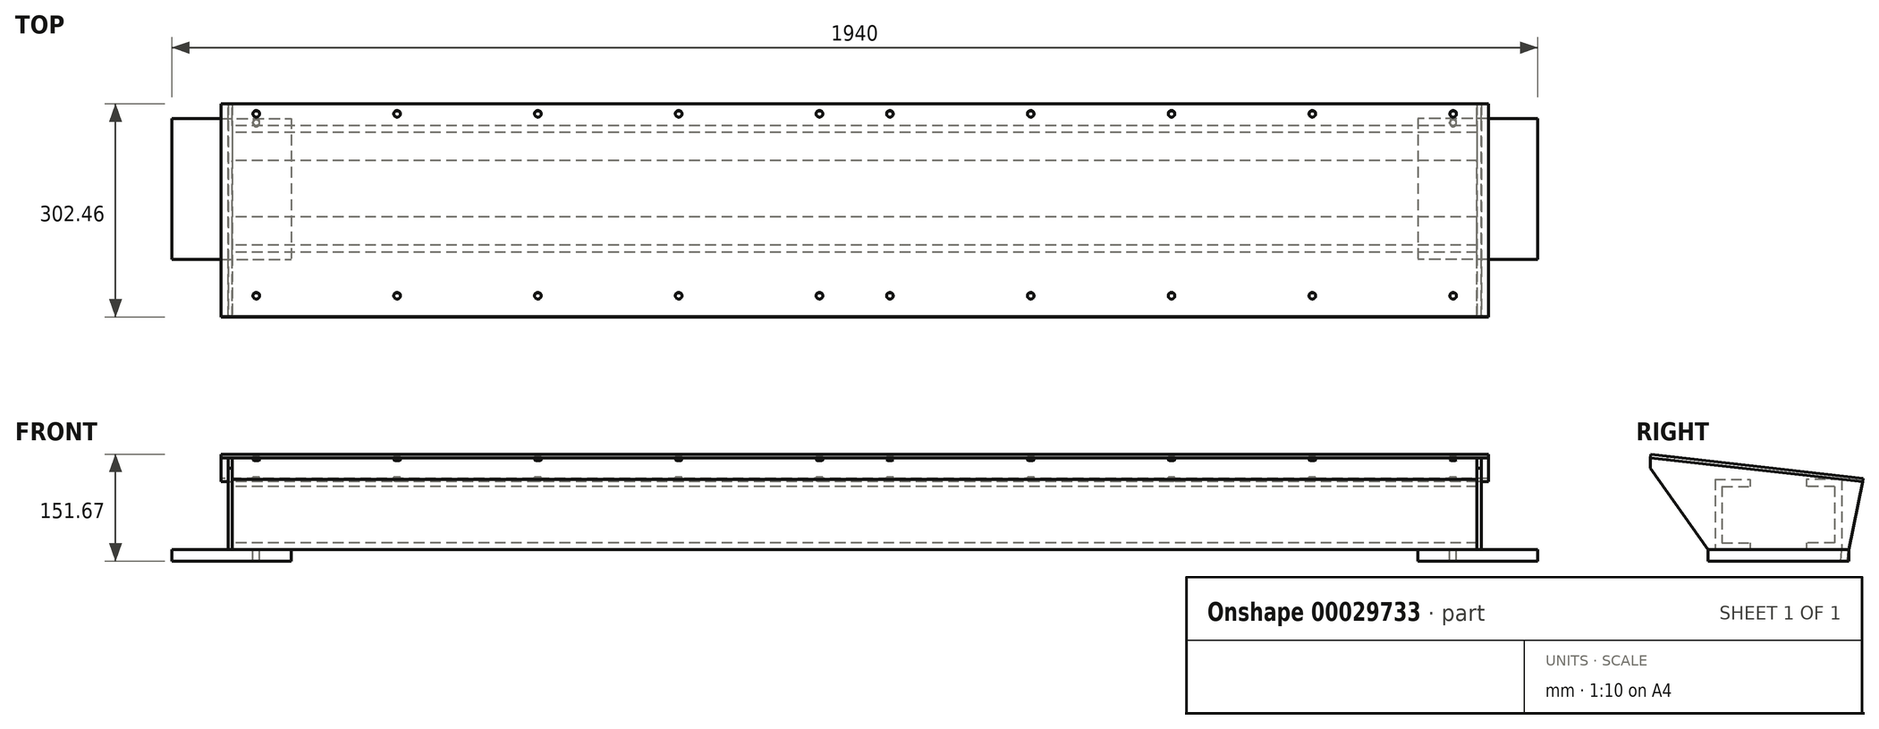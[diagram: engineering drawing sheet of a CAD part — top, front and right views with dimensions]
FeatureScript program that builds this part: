
annotation { "Feature Type Name" : "Feature", "Feature Type Description" : "" }
export const myFeature = defineFeature(function(context is Context, id is Id, definition is map)
    precondition{}
    {
        {
            var Q0;
            Q0=qCreatedBy(makeId("Top.planeOp"),FACE);
            var sketch = newSketch(context, id + "F0", { "sketchPlane" : qUnion([Q0])});
            skLineSegment(sketch, "E0", {"start": v(0, 85.67) * mm, "end": v(0, -88.89) * mm, "construction": true});
            skLineSegment(sketch, "E1.0", {"start": v(-800, 85.67) * mm, "end": v(-800, -88.89) * mm, "construction": true});
            skLineSegment(sketch, "E2.0", {"start": v(-970, 85.67) * mm, "end": v(-970, -88.89) * mm, "construction": true});
            skLineSegment(sketch, "E3", {"start": v(0, 0) * mm, "end": v(-970, 0) * mm, "construction": true});
            skLineSegment(sketch, "E4.0", {"start": v(0, 100) * mm, "end": v(-970, 100) * mm, "construction": true});
            skLineSegment(sketch, "E5.bottom", {"start": v(-970, 100) * mm, "end": v(-800, 100) * mm});
            skLineSegment(sketch, "E5.top", {"start": v(-970, -100) * mm, "end": v(-800, -100) * mm});
            skLineSegment(sketch, "E5.left", {"start": v(-970, 100) * mm, "end": v(-970, -100) * mm});
            skLineSegment(sketch, "E5.right", {"start": v(-800, 100) * mm, "end": v(-800, -100) * mm});
            skLineSegment(sketch, "E6.0", {"start": v(-950, 85.67) * mm, "end": v(-950, -88.89) * mm, "construction": true});
            skLineSegment(sketch, "E7.0", {"start": v(-959.5, 85.67) * mm, "end": v(-959.5, -88.89) * mm, "construction": true});
            skLineSegment(sketch, "E8.0", {"start": v(0, 65) * mm, "end": v(-970, 65) * mm, "construction": true});
            skLineSegment(sketch, "E9.0", {"start": v(0, 85) * mm, "end": v(-970, 85) * mm, "construction": true});
            skLineSegment(sketch, "E10.MirrorCS", {"start": v(800, 85.67) * mm, "end": v(800, -88.89) * mm});
            skLineSegment(sketch, "E11.MirrorCS", {"start": v(970, 85.67) * mm, "end": v(970, -88.89) * mm});
            skLineSegment(sketch, "E12.MirrorCS", {"start": v(970, 100) * mm, "end": v(800, 100) * mm});
            skLineSegment(sketch, "E13.MirrorCS", {"start": v(970, -100) * mm, "end": v(800, -100) * mm});
            skLineSegment(sketch, "E14.MirrorCS", {"start": v(970, 100) * mm, "end": v(970, -100) * mm});
            skLineSegment(sketch, "E15.MirrorCS", {"start": v(959.5, 85.67) * mm, "end": v(959.5, -88.89) * mm});
            skLineSegment(sketch, "E16.MirrorCS", {"start": v(950, 85.67) * mm, "end": v(950, -88.89) * mm});
            skLineSegment(sketch, "E17.MirrorCS", {"start": v(800, 100) * mm, "end": v(800, -100) * mm});
            skSolve(sketch);
        }
        {
            var Q0;
            Q0 = qSketchRegion(id + "F0", true);
            extrude(context, id + "F1", {"entities" : qUnion([Q0]), "oppositeDirection" : true, "depth" : 16 * mm});
        }
        {
            var Q0;
            Q0=qCreatedBy(makeId("Right.planeOp"),FACE);
            var sketch = newSketch(context, id + "F2", { "sketchPlane" : qUnion([Q0])});
            skLineSegment(sketch, "E18", {"start": v(0, 75.8) * mm, "end": v(0, -76.42) * mm, "construction": true});
            skLineSegment(sketch, "E19.0", {"start": v(100, 0) * mm, "end": v(-100, 0) * mm, "construction": true});
            skLineSegment(sketch, "E20.0", {"start": v(90, 100) * mm, "end": v(90, -76.42) * mm, "construction": true});
            skLineSegment(sketch, "E21.0", {"start": v(100, 100) * mm, "end": v(-100, 100) * mm, "construction": true});
            skLineSegment(sketch, "E22.bottom", {"start": v(90, 100) * mm, "end": v(40, 100) * mm});
            skLineSegment(sketch, "E22.top", {"start": v(90, 0) * mm, "end": v(40, 0) * mm});
            skLineSegment(sketch, "E22.left", {"start": v(90, 100) * mm, "end": v(90, 0) * mm});
            skLineSegment(sketch, "E22.right", {"start": v(40, 100) * mm, "end": v(40, 90) * mm});
            skLineSegment(sketch, "E23.0", {"start": v(80, 90) * mm, "end": v(40, 90) * mm});
            skLineSegment(sketch, "E23.1", {"start": v(80, 90) * mm, "end": v(80, 10) * mm});
            skLineSegment(sketch, "E23.2", {"start": v(80, 10) * mm, "end": v(40, 10) * mm});
            skLineSegment(sketch, "E24.trimOffspring", {"start": v(40, 10) * mm, "end": v(40, 0) * mm});
            skLineSegment(sketch, "E25.MirrorCS", {"start": v(-40, 100) * mm, "end": v(-40, 90) * mm});
            skLineSegment(sketch, "E26.MirrorCS", {"start": v(-40, 10) * mm, "end": v(-40, 0) * mm});
            skLineSegment(sketch, "E27.MirrorCS", {"start": v(-90, 100) * mm, "end": v(-40, 100) * mm});
            skLineSegment(sketch, "E28.MirrorCS", {"start": v(-90, 100) * mm, "end": v(-90, 0) * mm});
            skLineSegment(sketch, "E29.MirrorCS", {"start": v(-80, 90) * mm, "end": v(-40, 90) * mm});
            skLineSegment(sketch, "E30.MirrorCS", {"start": v(-80, 90) * mm, "end": v(-80, 10) * mm});
            skLineSegment(sketch, "E31.MirrorCS", {"start": v(-80, 10) * mm, "end": v(-40, 10) * mm});
            skLineSegment(sketch, "E32.MirrorCS", {"start": v(-90, 0) * mm, "end": v(-40, 0) * mm});
            skSolve(sketch);
        }
        {
            var Q0;
            Q0 = qSketchRegion(id + "F2", true);
            extrude(context, id + "F3", {"entities" : qUnion([Q0]), "endBound" : BoundingType.SYMMETRIC, "depth" : 1768 * mm});
        }
        {
            var Q0;
            Q0=makeQuery(id+"F3.opExtrude","CAP_FACE",FACE,{"disambiguationData":[OSD([sQuery(id+"F2.wireOp",EDGE,"E22.bottom"),sQuery(id+"F2.wireOp",EDGE,"E22.top"),sQuery(id+"F2.wireOp",EDGE,"E22.left"),sQuery(id+"F2.wireOp",EDGE,"E22.right"),sQuery(id+"F2.wireOp",EDGE,"E23.0"),sQuery(id+"F2.wireOp",EDGE,"E23.1"),sQuery(id+"F2.wireOp",EDGE,"E23.2"),sQuery(id+"F2.wireOp",EDGE,"E24.trimOffspring")])],"isStart":true});
            var sketch = newSketch(context, id + "F4", { "sketchPlane" : qUnion([Q0])});
            skLineSegment(sketch, "E33.0", {"start": v(-120, 100) * mm, "end": v(-120, 0) * mm, "construction": true});
            skLineSegment(sketch, "E34.0", {"start": v(181.9, 130.7) * mm, "end": v(181.9, 0) * mm, "construction": true});
            skLineSegment(sketch, "E35.0", {"start": v(-100, 0) * mm, "end": v(100, 0) * mm, "construction": true});
            skLineSegment(sketch, "E36.0", {"start": v(-100, 130.7) * mm, "end": v(181.9, 130.7) * mm, "construction": true});
            skLineSegment(sketch, "E37.0", {"start": v(-120, 96.6) * mm, "end": v(100, 96.6) * mm, "construction": true});
            skLineSegment(sketch, "E38", {"start": v(-120, 96.6) * mm, "end": v(181.9, 130.7) * mm, "construction": true});
            skLineSegment(sketch, "E39", {"start": v(181.9, 130.7) * mm, "end": v(224.8, 130.7) * mm, "construction": true});
            skLineSegment(sketch, "E40.0", {"start": v(181.9, 115.7) * mm, "end": v(224.8, 115.7) * mm, "construction": true});
            skLineSegment(sketch, "E41", {"start": v(-100, 0) * mm, "end": v(-120, 96.6) * mm});
            skLineSegment(sketch, "E42", {"start": v(-120, 96.6) * mm, "end": v(181.9, 130.7) * mm});
            skLineSegment(sketch, "E43", {"start": v(181.9, 130.7) * mm, "end": v(181.9, 115.7) * mm});
            skLineSegment(sketch, "E44", {"start": v(181.9, 115.7) * mm, "end": v(100, 0) * mm});
            skLineSegment(sketch, "E45", {"start": v(100, 0) * mm, "end": v(-100, 0) * mm});
            skSolve(sketch);
        }
        {
            var Q0;
            Q0 = qSketchRegion(id + "F4", true);
            extrude(context, id + "F5", {"entities" : qUnion([Q0]), "depth" : 6 * mm});
        }
        {
            var Q0;
            Q0=makeQuery(id+"F5.opExtrude","SWEPT_BODY",BODY,{"disambiguationData":[OSD([sQuery(id+"F4.wireOp",EDGE,"E41"),sQuery(id+"F4.wireOp",EDGE,"E42"),sQuery(id+"F4.wireOp",EDGE,"E43"),sQuery(id+"F4.wireOp",EDGE,"E44"),sQuery(id+"F4.wireOp",EDGE,"E45")])]});
            var Q1;
            Q1=qCreatedBy(makeId("Right.planeOp"),FACE);
            mirror(context, id + "F6", {"entities" : qUnion([Q0]), "mirrorPlane" : qUnion([Q1])});
        }
        {
            var Q0;
            Q0=qCreatedBy(makeId("Right.planeOp"),FACE);
            var sketch = newSketch(context, id + "F7", { "sketchPlane" : qUnion([Q0])});
            skLineSegment(sketch, "E46.0", {"start": v(120, 96.6) * mm, "end": v(-181.9, 130.7) * mm, "construction": true});
            skLineSegment(sketch, "E47.0", {"start": v(120.56, 101.57) * mm, "end": v(-181.34, 135.67) * mm});
            skLineSegment(sketch, "E48", {"start": v(120.56, 101.57) * mm, "end": v(120, 96.6) * mm});
            skLineSegment(sketch, "E49", {"start": v(-181.34, 135.67) * mm, "end": v(-181.9, 130.7) * mm});
            skLineSegment(sketch, "E50", {"start": v(120, 96.6) * mm, "end": v(-181.9, 130.7) * mm});
            skSolve(sketch);
        }
        {
            var Q0;
            Q0 = qSketchRegion(id + "F7", true);
            extrude(context, id + "F8", {"entities" : qUnion([Q0]), "operationType" : NewBodyOperationType.ADD, "endBound" : BoundingType.SYMMETRIC, "depth" : 1800 * mm});
        }
        {
            var Q0;
            Q0=makeQuery(id+"F8.opExtrude","SWEPT_FACE",FACE,{"disambiguationData":[OSD([sQuery(id+"F7.wireOp",EDGE,"E47.0")])]});
            var sketch = newSketch(context, id + "F9", { "sketchPlane" : qUnion([Q0])});
            skLineSegment(sketch, "E51.0", {"start": v(900, 94.4) * mm, "end": v(-900, 94.4) * mm, "construction": true});
            skLineSegment(sketch, "E52.0", {"start": v(900, -165.6) * mm, "end": v(-900, -165.6) * mm, "construction": true});
            skLineSegment(sketch, "E53", {"start": v(0, 214.6) * mm, "end": v(0, -296.2) * mm, "construction": true});
            skLineSegment(sketch, "E54.0", {"start": v(-50, 214.6) * mm, "end": v(-50, -296.2) * mm, "construction": true});
            skCircle(sketch, "E55", {"center": v(-50, 94.4) * mm, "radius": 4.75 * mm});
            skCircle(sketch, "E56.0.1.0", {"center": v(-50, -165.6) * mm, "radius": 4.75 * mm});
            skCircle(sketch, "E56.1.0.0", {"center": v(-250, 94.4) * mm, "radius": 4.75 * mm});
            skCircle(sketch, "E56.1.1.0", {"center": v(-250, -165.6) * mm, "radius": 4.75 * mm});
            skCircle(sketch, "E56.2.0.0", {"center": v(-450, 94.4) * mm, "radius": 4.75 * mm});
            skCircle(sketch, "E56.2.1.0", {"center": v(-450, -165.6) * mm, "radius": 4.75 * mm});
            skCircle(sketch, "E56.3.0.0", {"center": v(-650, 94.4) * mm, "radius": 4.75 * mm});
            skCircle(sketch, "E56.3.1.0", {"center": v(-650, -165.6) * mm, "radius": 4.75 * mm});
            skLineSegment(sketch, "E56.direction1", {"start": v(-50, 94.4) * mm, "end": v(-250, 94.4) * mm, "construction": true});
            skLineSegment(sketch, "E56.direction2", {"start": v(-50, 94.4) * mm, "end": v(-50, -165.6) * mm, "construction": true});
            skCircle(sketch, "E57.0.4.0", {"center": v(-850, 94.4) * mm, "radius": 4.75 * mm});
            skCircle(sketch, "E57.0.4.1", {"center": v(-850, -165.6) * mm, "radius": 4.75 * mm});
            skCircle(sketch, "E58.MirrorC", {"center": v(50, 94.4) * mm, "radius": 4.75 * mm});
            skCircle(sketch, "E59.MirrorC", {"center": v(250, 94.4) * mm, "radius": 4.75 * mm});
            skCircle(sketch, "E60.MirrorC", {"center": v(50, -165.6) * mm, "radius": 4.75 * mm});
            skCircle(sketch, "E61.MirrorC", {"center": v(650, -165.6) * mm, "radius": 4.75 * mm});
            skCircle(sketch, "E62.MirrorC", {"center": v(650, 94.4) * mm, "radius": 4.75 * mm});
            skCircle(sketch, "E63.MirrorC", {"center": v(450, -165.6) * mm, "radius": 4.75 * mm});
            skCircle(sketch, "E64.MirrorC", {"center": v(450, 94.4) * mm, "radius": 4.75 * mm});
            skCircle(sketch, "E65.MirrorC", {"center": v(250, -165.6) * mm, "radius": 4.75 * mm});
            skCircle(sketch, "E66.MirrorC", {"center": v(850, -165.6) * mm, "radius": 4.75 * mm});
            skCircle(sketch, "E67.MirrorC", {"center": v(850, 94.4) * mm, "radius": 4.75 * mm});
            skLineSegment(sketch, "E68.MirrorCS", {"start": v(50, 94.4) * mm, "end": v(250, 94.4) * mm});
            skLineSegment(sketch, "E69.MirrorCS", {"start": v(50, 94.4) * mm, "end": v(50, -165.6) * mm});
            skSolve(sketch);
        }
        {
            var Q0;
            Q0 = qSketchRegion(id + "F9", true);
            extrude(context, id + "F10", {"entities" : qUnion([Q0]), "operationType" : NewBodyOperationType.REMOVE, "endBound" : BoundingType.THROUGH_ALL, "oppositeDirection" : true, "depth" : 25 * mm});
        }
    });
